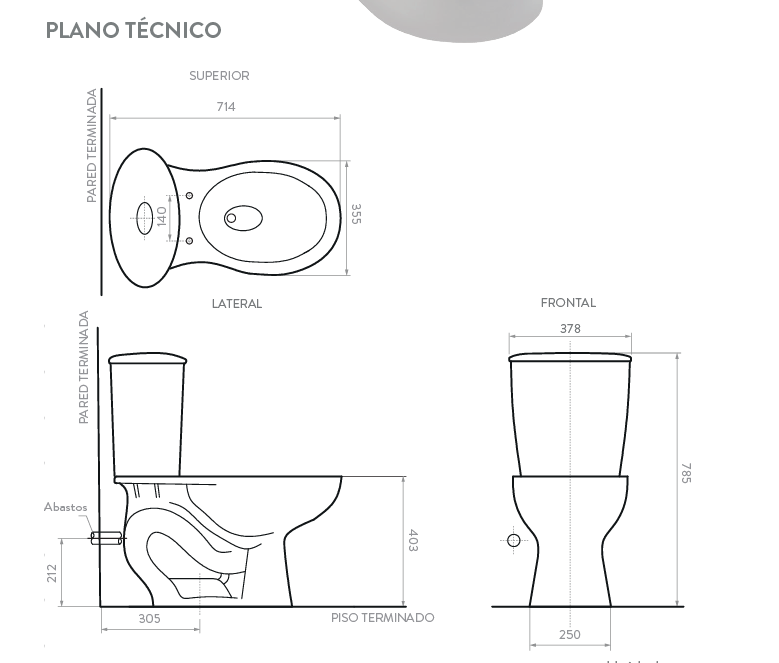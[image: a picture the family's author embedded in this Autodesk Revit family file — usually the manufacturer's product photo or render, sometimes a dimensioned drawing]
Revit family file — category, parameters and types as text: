
# Revit family: 121541001_Sanitario One Piece Burgos Al Bco
name_source: partatom
category: Plumbing Fixtures
units: mm (PartAtom-declared; Revit-internal decimal feet)

## family parameters
Always vertical = Yes
Cut with Voids When Loaded = No
OmniClass Number = 23.31.19.17
OmniClass Title = Toilets With Tank
Part Type = Normal
Room Calculation Point = No
Round Connector Dimension = Use Diameter
Shared = No
Work Plane-Based = No

## types (1)
- 121541001_Sanitario One Piece Burgos Al Bco
    Alto = 737 mm  [stored 2.41798 ft]
    Altura de Sello = 2 3/8Pulgadas(6 cm).
    Ancho = 391 mm
    Creado por = IDD
    Description = Capacidad de descarga de hasta 600 gr de miso.
    Dimensiones del Producto Empacado = 79 x 40,0 x 111
    Dimensiones generales del producto = 73,7cm x 39,1cm x 71,9cm
    Espejo de Agua = 18,5 cm x 21,3 cm .
    Fecha de creación = 13/08/2020
    Garantía = Garantía Integral de por vida.
    Manufacturer = CORONA
    Material = Corona_Porcelana_Sanitaria
    Material 2 = Corona_Aluminio
    Model = Sanitario One Piece Burgos Al Bco
    Peso Bruto aprox = 51,8 kg.
    Peso Neto aprox = 50,3 kg.
    Presion maxima = 20 - 80 PSI.
    Profundidad = 719 mm
    Sistema de Carga = Por gravedad
    URL = https://corona.co

note: [stored X ft] marks values corroborated as IEEE doubles in the binary element streams (Revit-internal decimal feet)

## geometry (parser evidence)
native form markers: Sweep x2
no freeform markers — native parametric forms only
